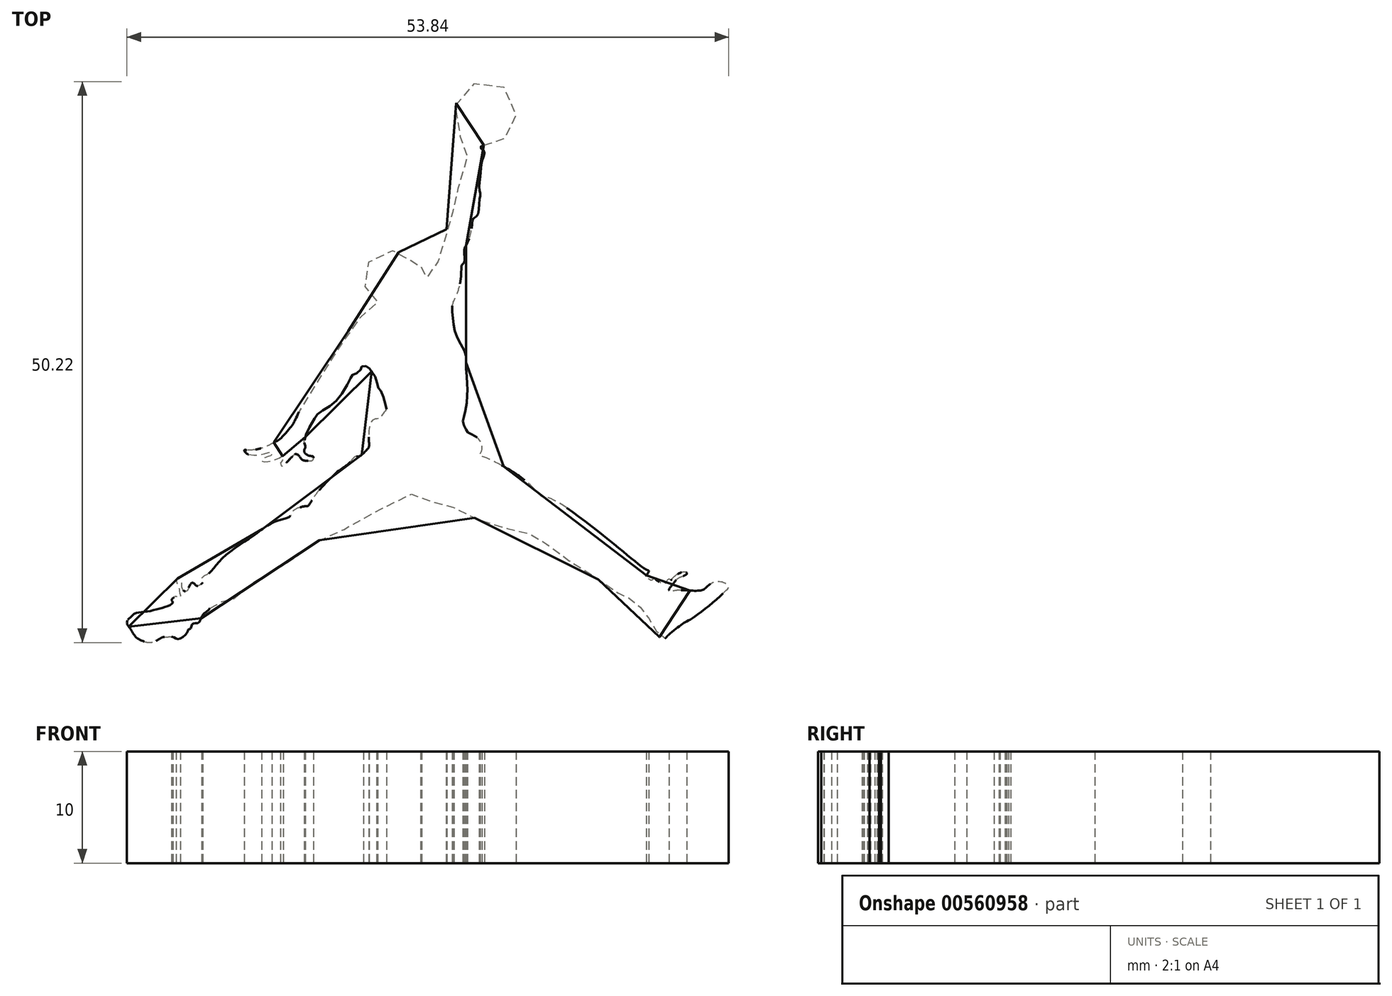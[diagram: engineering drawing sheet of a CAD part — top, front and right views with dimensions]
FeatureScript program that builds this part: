
annotation { "Feature Type Name" : "Feature", "Feature Type Description" : "" }
export const myFeature = defineFeature(function(context is Context, id is Id, definition is map)
    precondition{}
    {
        {
            var Q0;
            Q0=qCreatedBy(makeId("Top.planeOp"),FACE);
            var sketch = newSketch(context, id + "F0", { "sketchPlane" : qUnion([Q0])});
            skFitSpline(sketch, "E0", {"points": [v(33.14, 47.53) * mm, v(33.8, 47.62) * mm, v(34.48, 47.8) * mm, v(35.34, 48.42) * mm, v(35.87, 49.22) * mm, v(36.02, 50.58) * mm, v(35.64, 52.04) * mm, v(34.39, 52.99) * mm, v(33.02, 53.2) * mm, v(31.45, 52.6) * mm, v(30.74, 51.53) * mm, v(30.47, 50.2) * mm, v(30.83, 48.69) * mm, v(31.42, 47.5) * mm, v(31.48, 47.2) * mm, v(31.66, 46.7) * mm, v(31.07, 43.85) * mm, v(30.95, 43.79) * mm, v(30.65, 43.23) * mm, v(30.32, 41.8) * mm, v(30.35, 41.56) * mm, v(29.94, 40.76) * mm, v(29.76, 40.29) * mm, v(29.82, 39.6) * mm, v(29.64, 39.25) * mm, v(29.08, 37.2) * mm, v(28.73, 36.68) * mm, v(28.3, 36.32) * mm, v(28.06, 35.69) * mm, v(27.91, 35.62) * mm, v(27.8, 36.04) * mm, v(27.5, 36.29) * mm, v(27.53, 36.57) * mm, v(27.53, 36.82) * mm, v(26.93, 36.89) * mm, v(26.71, 37.1) * mm, v(26.47, 37.24) * mm, v(26.11, 37.63) * mm, v(25.7, 37.88) * mm, v(24.84, 38.09) * mm, v(23.79, 37.84) * mm, v(22.8, 37) * mm, v(22.44, 36.11) * mm, v(22.4, 35.09) * mm, v(22.97, 34.2) * mm, v(23.47, 33.75) * mm, v(23.64, 33.57) * mm, v(23.15, 32.69) * mm, v(22.55, 32.27) * mm, v(21.8, 31.95) * mm, v(21.02, 30.92) * mm, v(20.1, 29.14) * mm, v(19.89, 28.9) * mm, v(19.4, 28.24) * mm, v(19.1, 27.38) * mm, v(18.76, 26.99) * mm, v(17.84, 25.72) * mm, v(16.89, 24.24) * mm, v(16.22, 22.83) * mm, v(15.88, 22.3) * mm, v(14.8, 21.15) * mm, v(14.38, 20.92) * mm, v(13.57, 20.5) * mm, v(12, 20.21) * mm, v(11.7, 20.21) * mm, v(11.96, 19.88) * mm, v(13.22, 19.83) * mm, v(13.89, 20) * mm, v(14.13, 20.02) * mm, v(14.17, 19.77) * mm, v(13.98, 19.68) * mm, v(13.43, 19.47) * mm, v(13.25, 19.33) * mm, v(13.32, 19.2) * mm, v(13.66, 19.17) * mm, v(14.24, 19.3) * mm, v(14.91, 19.56) * mm, v(15.12, 19.7) * mm, v(15.16, 19.33) * mm, v(14.95, 19.07) * mm, v(15.09, 18.75) * mm, v(15.46, 19.05) * mm, v(15.83, 19.47) * mm, v(16.1, 19.74) * mm, v(16.25, 19.86) * mm, v(16.57, 19.74) * mm, v(16.89, 19.35) * mm, v(17.43, 19.26) * mm, v(17.8, 19.31) * mm, v(17.9, 19.6) * mm, v(17.52, 19.72) * mm, v(17.13, 19.95) * mm, v(17.06, 20.21) * mm, v(17.17, 20.48) * mm, v(17.08, 20.88) * mm, v(17.15, 21.36) * mm, v(17.47, 22.17) * mm, v(18.14, 23.28) * mm, v(18.28, 23.46) * mm, v(18.99, 23.94) * mm, v(19.85, 24.55) * mm, v(20.73, 25.72) * mm, v(21.23, 26.74) * mm, v(21.28, 26.87) * mm, v(21.54, 27.04) * mm, v(21.84, 27.15) * mm, v(22.14, 27.47) * mm, v(22.18, 27.66) * mm, v(22.36, 27.73) * mm, v(22.62, 27.75) * mm, v(22.87, 27.57) * mm, v(23.6, 26.4) * mm, v(23.56, 26.14) * mm, v(23.8, 25.65) * mm, v(23.93, 25.53) * mm, v(24.14, 24.98) * mm, v(24.4, 24.1) * mm, v(24.42, 23.87) * mm, v(24.2, 23.58) * mm, v(23.94, 23.2) * mm, v(23.79, 23.05) * mm, v(23.27, 22.95) * mm, v(22.94, 22.44) * mm, v(22.83, 21.52) * mm, v(22.85, 20.5) * mm, v(22.66, 20.23) * mm, v(21.99, 19.67) * mm, v(21.6, 19.61) * mm, v(21.16, 19.12) * mm, v(20.23, 18.43) * mm, v(18.87, 17.13) * mm, v(17.92, 16) * mm, v(17.42, 15.22) * mm, v(17.25, 15.2) * mm, v(16.5, 15.03) * mm, v(15.93, 14.6) * mm, v(15.78, 14.3) * mm, v(14.35, 13.77) * mm, v(12.63, 12.64) * mm, v(9.82, 10.6) * mm, v(8.48, 9.15) * mm, v(7.9, 8.75) * mm, v(7.98, 8.5) * mm, v(7.93, 8.3) * mm, v(7.56, 8.06) * mm, v(7.37, 8.1) * mm, v(7.07, 8.36) * mm, v(6.72, 7.87) * mm, v(6.55, 7.6) * mm, v(6.32, 7.6) * mm, v(6.13, 7.94) * mm, v(6.02, 8.6) * mm, v(5.69, 8.71) * mm, v(5.65, 8.4) * mm, v(5.81, 8.1) * mm, v(5.88, 7.81) * mm, v(5.96, 7.3) * mm, v(5.96, 7) * mm, v(5.65, 7.1) * mm, v(5.46, 7.08) * mm, v(5.2, 6.78) * mm, v(5.31, 6.6) * mm, v(4.95, 6.3) * mm, v(4.03, 6) * mm, v(2.81, 5.73) * mm, v(1.97, 5.6) * mm, v(1.43, 5.17) * mm, v(1.26, 4.98) * mm, v(1.22, 4.66) * mm, v(1.56, 4.16) * mm, v(2.06, 3.43) * mm, v(2.88, 3.05) * mm, v(3.36, 3) * mm, v(4.03, 3.26) * mm, v(4.47, 3.49) * mm, v(4.74, 3.49) * mm, v(5.31, 3.49) * mm, v(5.73, 3.3) * mm, v(6.32, 3.57) * mm, v(6.63, 4) * mm, v(6.72, 4.18) * mm, v(6.86, 4.2) * mm, v(7.03, 4.58) * mm, v(7.2, 4.7) * mm, v(7.62, 4.77) * mm, v(7.98, 5.44) * mm, v(8.52, 5.92) * mm, v(8.75, 6.28) * mm, v(9.17, 6.47) * mm, v(9.5, 6.53) * mm, v(10.24, 7.03) * mm, v(10.39, 7.1) * mm, v(10.62, 6.95) * mm, v(10.83, 6.95) * mm, v(11.44, 7.47) * mm, v(13.66, 9.15) * mm, v(16.16, 10.48) * mm, v(18.82, 12.4) * mm, v(20.27, 12.97) * mm, v(23.34, 14.6) * mm, v(26.31, 16.16) * mm, v(26.92, 16.29) * mm, v(27.43, 16.04) * mm, v(28.52, 15.6) * mm, v(29.67, 15.34) * mm, v(31.41, 14.63) * mm, v(32.71, 13.96) * mm, v(34.7, 13.33) * mm, v(36.28, 12.97) * mm, v(37.04, 12.83) * mm, v(37.83, 12.32) * mm, v(38.59, 11.92) * mm, v(39.93, 10.9) * mm, v(41.28, 9.97) * mm, v(42.4, 9.22) * mm, v(42.74, 9.15) * mm, v(43.29, 8.71) * mm, v(44.17, 8.08) * mm, v(44.67, 7.62) * mm, v(44.99, 7.45) * mm, v(45.47, 7.4) * mm, v(45.68, 7.41) * mm, v(45.9, 7.2) * mm, v(46.23, 6.89) * mm, v(46.48, 6.64) * mm, v(46.84, 6.3) * mm, v(47.28, 6.03) * mm, v(47.38, 5.71) * mm, v(47.7, 5.36) * mm, v(48.07, 4.98) * mm, v(48.37, 4.6) * mm, v(48.53, 4.1) * mm, v(48.7, 3.72) * mm, v(49, 3.32) * mm, v(49.33, 3.32) * mm, v(49.54, 3.55) * mm, v(50.36, 4.24) * mm, v(51.12, 4.79) * mm, v(52.02, 5.31) * mm, v(55, 7.85) * mm, v(55.02, 8.02) * mm, v(54.51, 8.38) * mm, v(53.57, 8.31) * mm, v(53.09, 7.96) * mm, v(52.65, 7.68) * mm, v(51.6, 7.64) * mm, v(50.4, 7.66) * mm, v(49.84, 7.6) * mm, v(49.7, 7.73) * mm, v(50.15, 8.34) * mm, v(50.57, 8.78) * mm, v(51.28, 9.11) * mm, v(51.26, 9.26) * mm, v(50.63, 9.2) * mm, v(49.94, 8.65) * mm, v(49.9, 8.59) * mm, v(49.65, 8.65) * mm, v(49.31, 8.25) * mm, v(48.4, 8.67) * mm, v(48.26, 8.65) * mm, v(48.1, 8.57) * mm, v(47.67, 8.92) * mm, v(47.72, 9.07) * mm, v(47.9, 9.38) * mm, v(47.7, 9.51) * mm, v(46.52, 10.37) * mm, v(43.2, 13.08) * mm, v(38.97, 15.93) * mm, v(38.42, 16.01) * mm, v(37.9, 16.5) * mm, v(36.72, 17.59) * mm, v(34.94, 18.74) * mm, v(32.92, 19.69) * mm, v(32.75, 19.76) * mm, v(32.92, 20.09) * mm, v(32.95, 20.7) * mm, v(32.55, 21.33) * mm, v(31.75, 21.78) * mm, v(31.53, 22.08) * mm, v(31.25, 22.73) * mm, v(31.4, 23.33) * mm, v(31.65, 25.05) * mm, v(31.65, 26.15) * mm, v(31.55, 27.95) * mm, v(31.48, 28.94) * mm, v(30.68, 30.47) * mm, v(30.4, 31.74) * mm, v(30.3, 32.99) * mm, v(30.58, 33.88) * mm, v(30.9, 34.68) * mm, v(31.08, 35.68) * mm, v(31.13, 36.5) * mm, v(31.18, 36.8) * mm, v(31.38, 37.05) * mm, v(31.38, 38.05) * mm, v(31.5, 38.48) * mm, v(31.93, 39.47) * mm, v(32.1, 40.65) * mm, v(32.15, 40.9) * mm, v(32.3, 41.02) * mm, v(32.6, 41.3) * mm, v(32.75, 42.52) * mm, v(32.82, 43.14) * mm, v(32.75, 43.5) * mm, v(32.8, 44.61) * mm, v(32.9, 45.61) * mm, v(33.05, 46.34) * mm, v(33.15, 47) * mm, v(32.82, 47.3) * mm, v(33.14, 47.53) * mm]});
            skSolve(sketch);
        }
        {
            var Q0;
            Q0=makeQuery(id+"F0.imprint","IMPRINT",FACE,{"disambiguationData":[TD([[makeQuery(id+"F0.imprint","IMPRINT",EDGE,{"derivedFrom":sQuery(id+"F0.wireOp",EDGE,"E0")}),1.0]])]});
            extrude(context, id + "F1", {"entities" : qUnion([Q0]), "depth" : 10 * mm, "offsetDistance" : 25 * mm});
        }
    });
